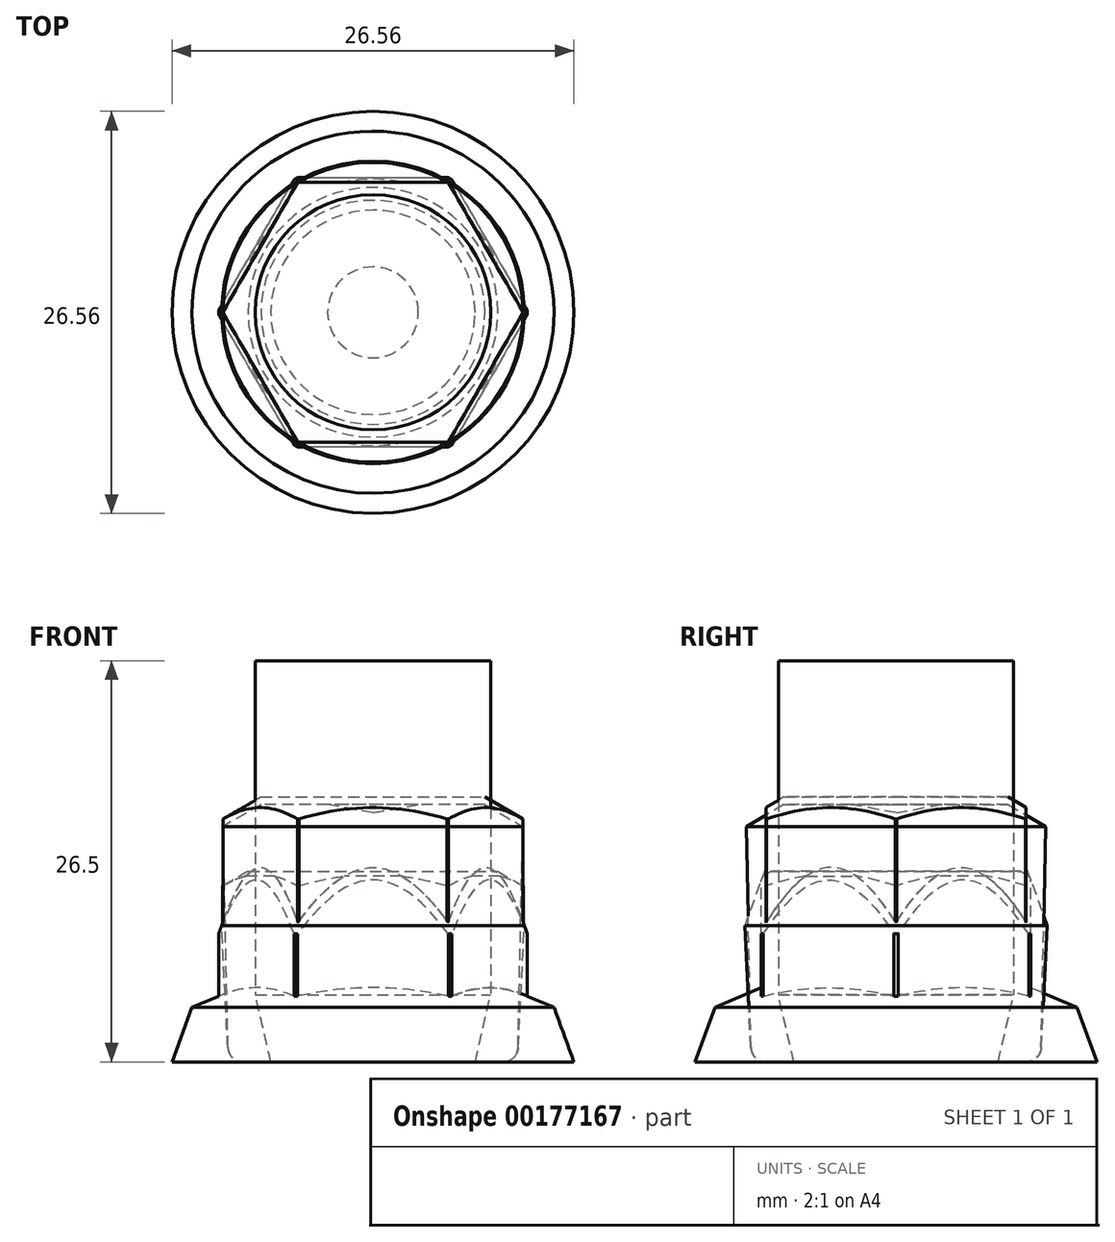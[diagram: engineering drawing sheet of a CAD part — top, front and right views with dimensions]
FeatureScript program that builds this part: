
annotation { "Feature Type Name" : "Feature", "Feature Type Description" : "" }
export const myFeature = defineFeature(function(context is Context, id is Id, definition is map)
    precondition{}
    {
        {
            var Q0;
            Q0=qCreatedBy(makeId("Front.planeOp"),FACE);
            var sketch = newSketch(context, id + "F0", { "sketchPlane" : qUnion([Q0]), "disableImprinting" : false});
            skLineSegment(sketch, "E0", {"start": v(0, 0) * mm, "end": v(0, 12.6) * mm});
            skLineSegment(sketch, "E1", {"start": v(0, 12.6) * mm, "end": v(8.25, 12.6) * mm});
            skLineSegment(sketch, "E2", {"start": v(10.2, 11.47) * mm, "end": v(10.2, 4.35) * mm});
            skLineSegment(sketch, "E3", {"start": v(10.2, 4.35) * mm, "end": v(14.56, 2.5) * mm});
            skLineSegment(sketch, "E4", {"start": v(15, 2.31) * mm, "end": v(15, 0) * mm, "construction": true});
            skLineSegment(sketch, "E5", {"start": v(14.56, 0) * mm, "end": v(0, 0) * mm});
            skLineSegment(sketch, "E6", {"start": v(8.25, 12.6) * mm, "end": v(10.2, 11.47) * mm});
            skLineSegment(sketch, "E7", {"start": v(0, 0) * mm, "end": v(0, 12.6) * mm, "construction": true});
            skArc(sketch, "E8", {"start": v(14.56, 0) * mm, "mid": v(15, 1.25) * mm, "end": v(14.56, 2.5) * mm});
            skSolve(sketch);
        }
        {
            var Q0;
            Q0=qSketchRegion(id+"F0",true);
            var Q1;
            Q1=sQuery(id+"F0.wireOp",EDGE,"E0");
            revolve(context, id + "F1", {"entities" : qUnion([Q0]), "axis" : qUnion([Q1]), "revolveType" : RevolveType.FULL});
        }
        {
            var Q0;
            Q0=makeQuery(id+"F1.opRevolve","SWEPT_FACE",FACE,{"disambiguationData":[OSD([sQuery(id+"F0.wireOp",EDGE,"E1")])]});
            var sketch = newSketch(context, id + "F2", { "sketchPlane" : qUnion([Q0])});
            skCircle(sketch, "E9.cCircle", {"center": v(0, 0) * mm, "radius": 8.9 * mm, "construction": true});
            skLineSegment(sketch, "E9.0", {"start": v(-5.14, 8.9) * mm, "end": v(5.14, 8.9) * mm});
            skLineSegment(sketch, "E9.1", {"start": v(5.14, 8.9) * mm, "end": v(10.28, 0) * mm});
            skLineSegment(sketch, "E9.2", {"start": v(10.28, 0) * mm, "end": v(5.14, -8.9) * mm});
            skLineSegment(sketch, "E9.3", {"start": v(5.14, -8.9) * mm, "end": v(-5.14, -8.9) * mm});
            skLineSegment(sketch, "E9.4", {"start": v(-5.14, -8.9) * mm, "end": v(-10.28, 0) * mm});
            skLineSegment(sketch, "E9.5", {"start": v(-10.28, 0) * mm, "end": v(-5.14, 8.9) * mm});
            skPoint(sketch, "E9.0.midPoint", {"position": v(0, 8.9) * mm});
            skCircle(sketch, "E10", {"center": v(0, 0) * mm, "radius": 17.28 * mm});
            skSolve(sketch);
        }
        {
            var Q0;
            Q0=qSketchRegion(id+"F2",true);
            var Q1;
            Q1=makeQuery(id+"F1.opRevolve","SWEPT_FACE",FACE,{"disambiguationData":[OSD([sQuery(id+"F0.wireOp",EDGE,"E3")])]});
            extrude(context, id + "F3", {"entities" : qUnion([Q0]), "operationType" : NewBodyOperationType.REMOVE, "endBound" : BoundingType.UP_TO_SURFACE, "oppositeDirection" : true, "endBoundEntityFace" : qUnion([Q1]), "depth" : 25 * mm, "offsetDistance" : 25 * mm});
        }
        {
            var Q0;
            Q0=qCreatedBy(makeId("Front.planeOp"),FACE);
            var sketch = newSketch(context, id + "F4", { "sketchPlane" : qUnion([Q0])});
            skLineSegment(sketch, "E11", {"start": v(0, 0) * mm, "end": v(0, 17.5) * mm});
            skLineSegment(sketch, "E12", {"start": v(0, 17.5) * mm, "end": v(7.4, 17.5) * mm});
            skLineSegment(sketch, "E13", {"start": v(9.9, 16.06) * mm, "end": v(9.9, 9.27) * mm});
            skLineSegment(sketch, "E14", {"start": v(9.9, 9.27) * mm, "end": v(10, 9) * mm});
            skLineSegment(sketch, "E15", {"start": v(8.6, 0) * mm, "end": v(0, 0) * mm});
            skLineSegment(sketch, "E16", {"start": v(7.4, 17.5) * mm, "end": v(9.9, 16.06) * mm});
            skLineSegment(sketch, "E17", {"start": v(0, 0) * mm, "end": v(0, 17.5) * mm, "construction": true});
            skLineSegment(sketch, "E18", {"start": v(10, 9) * mm, "end": v(9.6, 0.95) * mm});
            skPoint(sketch, "E19.visualSharp", {"position": v(9.55, 0) * mm});
            skArc(sketch, "E19.filletArc", {"start": v(8.6, 0) * mm, "mid": v(9.3, 0.28) * mm, "end": v(9.6, 0.95) * mm});
            skSolve(sketch);
        }
        {
            var Q0;
            Q0 = qSketchRegion(id + "F4", true);
            var Q1;
            Q1=sQuery(id+"F4.wireOp",EDGE,"E11");
            revolve(context, id + "F5", {"surfaceOperationType" : NewSurfaceOperationType.NEW, "entities" : qUnion([Q0]), "axis" : qUnion([Q1]), "revolveType" : RevolveType.FULL});
        }
        {
            var Q0;
            Q0=makeQuery(id+"F5.opRevolve","SWEPT_FACE",FACE,{"disambiguationData":[OSD([sQuery(id+"F4.wireOp",EDGE,"E12")])]});
            var sketch = newSketch(context, id + "F6", { "sketchPlane" : qUnion([Q0])});
            skCircle(sketch, "E20.cCircle", {"center": v(0, 0) * mm, "radius": 8.6 * mm, "construction": true});
            skLineSegment(sketch, "E20.0", {"start": v(-4.97, 8.6) * mm, "end": v(4.97, 8.6) * mm});
            skLineSegment(sketch, "E20.1", {"start": v(4.97, 8.6) * mm, "end": v(9.93, 0) * mm});
            skLineSegment(sketch, "E20.2", {"start": v(9.93, 0) * mm, "end": v(4.97, -8.6) * mm});
            skLineSegment(sketch, "E20.3", {"start": v(4.97, -8.6) * mm, "end": v(-4.97, -8.6) * mm});
            skLineSegment(sketch, "E20.4", {"start": v(-4.97, -8.6) * mm, "end": v(-9.93, 0) * mm});
            skLineSegment(sketch, "E20.5", {"start": v(-9.93, 0) * mm, "end": v(-4.97, 8.6) * mm});
            skPoint(sketch, "E20.0.midPoint", {"position": v(0, 8.6) * mm});
            skCircle(sketch, "E21", {"center": v(0, 0) * mm, "radius": 16.7 * mm});
            skSolve(sketch);
        }
        {
            var Q0;
            Q0 = qSketchRegion(id + "F6", true);
            var Q1;
            Q1=makeQuery(id+"F5.opRevolve","SWEPT_FACE",FACE,{"disambiguationData":[OSD([sQuery(id+"F4.wireOp",EDGE,"E14")])]});
            extrude(context, id + "F7", {"entities" : qUnion([Q0]), "operationType" : NewBodyOperationType.REMOVE, "endBound" : BoundingType.UP_TO_SURFACE, "oppositeDirection" : true, "depth" : 25 * mm, "endBoundEntityFace" : qUnion([Q1]), "offsetDistance" : 25 * mm});
        }
        {
            var Q0;
            Q0=qCreatedBy(makeId("Front.planeOp"),FACE);
            var sketch = newSketch(context, id + "F8", { "sketchPlane" : qUnion([Q0])});
            skLineSegment(sketch, "E22", {"start": v(0, 0) * mm, "end": v(0, 16.47) * mm, "construction": true});
            skLineSegment(sketch, "E23", {"start": v(3, 17) * mm, "end": v(7.4, 17) * mm});
            skLineSegment(sketch, "E24", {"start": v(7.4, 17) * mm, "end": v(9.9, 15.56) * mm});
            skLineSegment(sketch, "E25", {"start": v(8.58, 0) * mm, "end": v(0, 0) * mm});
            skLineSegment(sketch, "E26", {"start": v(0, 16.47) * mm, "end": v(0, 0) * mm});
            skLineSegment(sketch, "E27", {"start": v(9.9, 15.56) * mm, "end": v(9.58, 0.98) * mm});
            skPoint(sketch, "E28.visualSharp", {"position": v(9.56, 0) * mm});
            skArc(sketch, "E28.filletArc", {"start": v(8.58, 0) * mm, "mid": v(9.28, 0.29) * mm, "end": v(9.58, 0.98) * mm});
            skLineSegment(sketch, "E29", {"start": v(3, 17) * mm, "end": v(0, 16.47) * mm});
            skSolve(sketch);
        }
        {
            var Q0;
            Q0=qSketchRegion(id+"F8",true);
            var Q1;
            Q1=sQuery(id+"F8.wireOp",EDGE,"E26");
            revolve(context, id + "F9", {"surfaceOperationType" : NewSurfaceOperationType.NEW, "entities" : qUnion([Q0]), "axis" : qUnion([Q1]), "revolveType" : RevolveType.FULL});
        }
        {
            var Q0;
            Q0=qCreatedBy(makeId("Front.planeOp"),FACE);
            var sketch = newSketch(context, id + "F10", { "sketchPlane" : qUnion([Q0])});
            skLineSegment(sketch, "E30", {"start": v(0, 0) * mm, "end": v(0, 26.5) * mm});
            skLineSegment(sketch, "E31", {"start": v(0, 26.5) * mm, "end": v(7.78, 26.5) * mm});
            skLineSegment(sketch, "E32", {"start": v(7.78, 26.5) * mm, "end": v(7.78, 4.44) * mm});
            skLineSegment(sketch, "E33", {"start": v(7.78, 4.44) * mm, "end": v(6.75, 0) * mm});
            skLineSegment(sketch, "E34", {"start": v(6.75, 0) * mm, "end": v(0, 0) * mm});
            skLineSegment(sketch, "E35", {"start": v(0, 26.5) * mm, "end": v(0, 0) * mm, "construction": true});
            skSolve(sketch);
        }
        {
            var Q0;
            Q0=qSketchRegion(id+"F10",true);
            var Q1;
            Q1=sQuery(id+"F10.wireOp",EDGE,"E30");
            revolve(context, id + "F11", {"surfaceOperationType" : NewSurfaceOperationType.NEW, "entities" : qUnion([Q0]), "axis" : qUnion([Q1]), "revolveType" : RevolveType.FULL});
        }
    });
